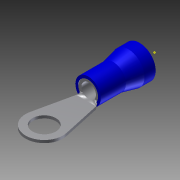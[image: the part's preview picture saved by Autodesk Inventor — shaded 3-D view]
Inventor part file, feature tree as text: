
AUTODESK INVENTOR PART (.ipt)
format: ipt  version: 2011 (Build 150239000, 239)  size: 131,072 bytes
history: native  units: mm
features: other x4, plane x2, imported_body x1, sketch x1
ambient origin geometry x8: Origin, YZ Plane, XZ Plane, XY Plane, X Axis, Y Axis, Z Axis, Center Point
bodies: Solid1 (feature_tree)
feature tree (8):
  imported_body  "Base1"
  sketch  "Sketch1"  dims[d0=3.175mm d1=6.35mm]
  other  "Work Point2"
  other  "Work Point3"
  plane  "Work Plane1"
  other  "Work Axis1"
  plane  "Work Plane2"
  other  "Work Axis2"
